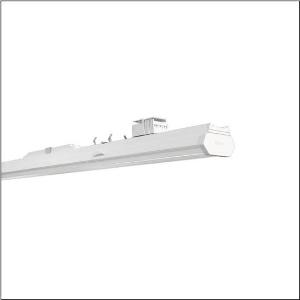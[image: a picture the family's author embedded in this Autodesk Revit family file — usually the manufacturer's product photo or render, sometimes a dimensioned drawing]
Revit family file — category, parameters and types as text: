
# Revit family: licross_11_protected_mo_51td1bdn49xg3c
name_source: partatom
category: Lighting Fixtures
units: mm (PartAtom-declared; Revit-internal decimal feet)

## family parameters
Cut with Voids When Loaded = No
Host = Face
Light Source = No
Part Type = Normal
Room Calculation Point = No
Round Connector Dimension = Use Diameter
Shared = No

## types (1)
- --- (1 x LED, 920 lm, 6.8 W, 4000K)
    Apparent Load = 7 VA
    CIE Flux Codes = 54 82 95 97 100
    Color Rendering = 80
    Color Temperature = 4000K
    Default Elevation = 1800 mm
    Description = Licross 11 Protected MO, luminaire insert, of sheet steel, galvanised, coil coated, white, length: 1.500mm, width: 90mm, height: 101mm, LED rated luminous flux: 9.370lm, light colour: 840, SDCM (Standard Deviation of Colour Matching)MacAdam ≤ 2 SDCM (initial), control gear: DALI 2 (for two DALI lines), with plug, 6-pole, with phase selection, for trunking rail, 14-core, mains connection: 220..240V, AC, 50/60Hz, rated input power: 61W, for trunking rail, 14-core, internal wiring halogen-free, for emergency light function, converter,control gear: single battery element, battery: LiFePO4, 9Ah, primary optical cover: cover, of PMMA, light emission: direct distribution, primary light characteristic: symmetric, protection rating (complete): IP54, insulation class (complete): insulation class I (protective earthing), certification: CE, UKCA, protection symbol: D if used in an environment with non-conductive dust loads with corresponding accessories, impact resistance: IK06, permissible ambient temperature for indoor applications: +5..+35°C, standard: EN 60598-2-22, LABS conformity tested according to VDMA 24364:2018-05, reducing of maximum allowable ambient temperature of 5°C with ceiling mounting, corresponds to IFS (International Featured Standards) requirements for safety and quality in the food industry, The light source and the operating device comply with the requirements of the Ecodesign Regulation (EU) 2019/2020 and are replaceable in accordance with this regulation, packaging unit: 1 piece
    Height = 92 mm
    Lamp = 1 x LED
    Lamp Light Flux = 920 lm
    Lamp Power = 6.8 W
    Lamp count = 1
    Length = 1500 mm
    Luminous efficacy = 135 lm/W
    Manufacturer = Siteco
    ModVariant = No
    Model = 51TD1BDN49XG3C
    Mounting Place = Ceiling
    Mounting Type = Pendant
    Number of Poles = 1
    OnlyDefault = Yes
    Power Factor = 1
    Product Name = Licross 11 Protected MO
    Product group = luminaire insert | ceiling pendant
    ProductGroupID = 901
    Protection Class = Protection class I
    Protection Degree = IP 54
    RLX_Detail_Level = 1
    RLX_Emergency_Light_Flux = 0 lm
    RLX_Emergency_Type = 0
    RLX_Emergency_Type_DB = No
    RlxData = <blob elided: 24885 chars, md5=e1858c99>
    Socket = socket
    Standby Power = 0 W
    System Light Flux = 920 lm
    System Power = 7 W
    Type Comments = : emergency light operation: 3 h
    Type Image = l_1256145.jpg
    URL = http://relux.com
    VarID = @adj_096563
    Voltage = 0 V
    Weight = 0.00 kg
    Width = 88 mm

## geometry (parser evidence)
native form markers: Blend x4, Sweep x9
no freeform markers — native parametric forms only
